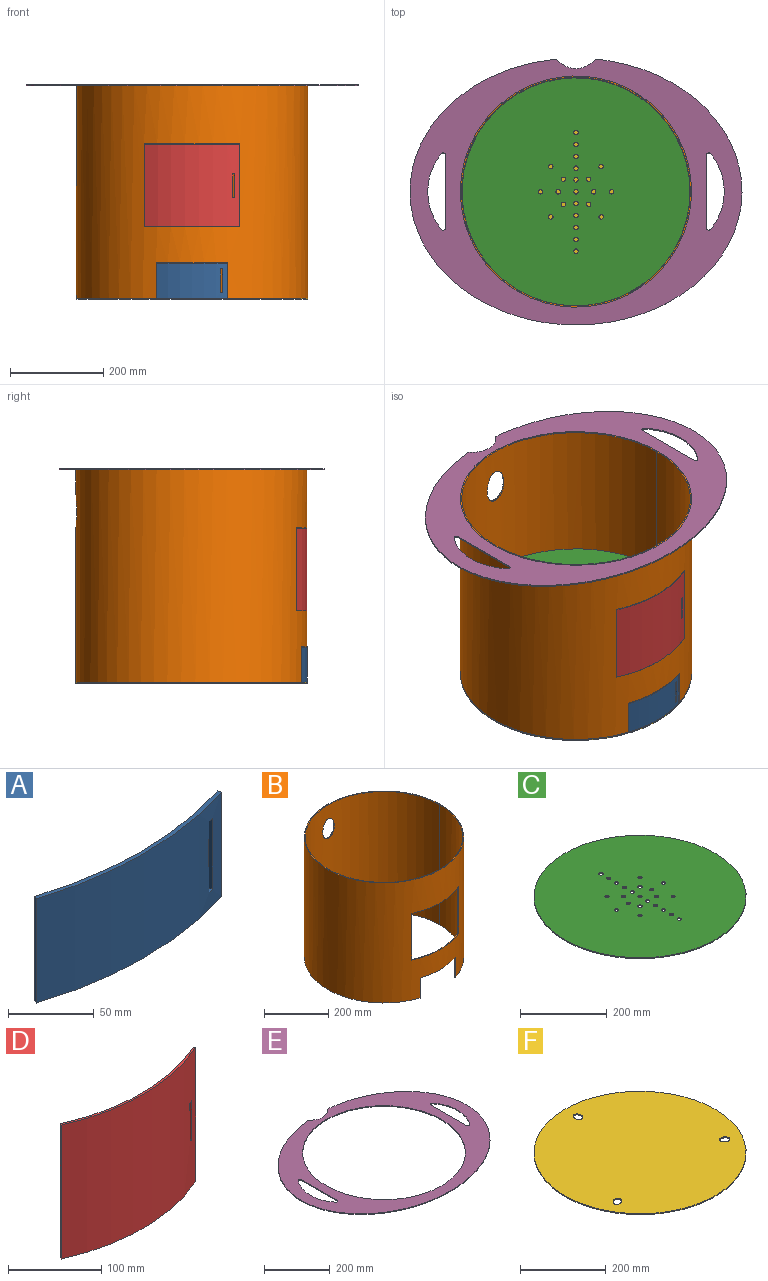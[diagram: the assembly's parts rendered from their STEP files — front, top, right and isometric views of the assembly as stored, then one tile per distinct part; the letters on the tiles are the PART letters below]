
ASSEMBLY  parts=6 mates=6
PART A: 10 faces, bbox 152.5x14.6x74.6 mm
  f0: plane 152.53x14.56mm, normal (0,0,-1), area 409.4mm2, adj f1,f7,f8,f9
  f1: plane 74.61x2.53mm, normal (0.95,0.31,0), area 198mm2, adj f0,f2,f8,f9
  f2: plane 152.53x14.56mm, normal (0,0,1), area 409.4mm2, adj f1,f7,f8,f9
  f3: plane 4.54x3.59mm, normal (0,0,-1), area 10.6mm2, adj f4,f6,f8,f9
  f4: plane 50.8x2.56mm, normal (-0.96,-0.27,0), area 134.8mm2, adj f3,f5,f8,f9
  f5: plane 4.54x3.59mm, normal (0,0,1), area 10.6mm2, adj f4,f6,f8,f9
  f6: plane 50.8x2.57mm, normal (0.97,0.25,0), area 134.8mm2, adj f3,f5,f8,f9
  f7: plane 74.61x2.53mm, normal (-0.95,0.31,0), area 198mm2, adj f0,f2,f8,f9
  f8: cylinder r=247.65mm len=152.53mm, axis (0,0,1), area 11365mm2, adj f0,f1,f2,f3,f4,f5,f6,f7
  f9: cylinder r=245mm len=150.9mm, axis (0,0,1), area 11243.2mm2, adj f0,f1,f2,f3,f4,f5,f6,f7
PART B: 18 faces, bbox 495.3x495.3x457.2 mm
  f0: plane 76.2x2.52mm, normal (0.95,-0.31,0), area 202.3mm2, adj f1,f15,f16,f17
  f1: plane 495.3x483.02mm, normal (0,0,-1), area 2873.6mm2, adj f0,f2,f16,f17
  f2: plane 457.2x2.65mm, normal (0,-1,0), area 1213.5mm2, adj f1,f3,f16,f17
  f3: plane 495.3x495.3mm, normal (0,0,1), area 4107.4mm2, adj f2,f4,f16,f17
  f4: plane 457.2x2.65mm, normal (0,1,0), area 1213.5mm2, adj f3,f5,f16,f17
  f5: plane 235.37x171.45mm, normal (0,0,-1), area 820.2mm2, adj f4,f6,f16,f17
  f6: plane 76.2x2.52mm, normal (-0.95,-0.31,0), area 202.3mm2, adj f5,f15,f16,f17
  f7: plane 205.4x24.71mm, normal (0,0,1), area 559.2mm2, adj f8,f14,f16,f17
  f8: plane 177.8x2.42mm, normal (-0.91,-0.41,0), area 471.9mm2, adj f7,f9,f16,f17
  f9: plane 205.4x24.71mm, normal (0,0,-1), area 559.2mm2, adj f8,f14,f16,f17
  f10: bspline ~51.37x40.16mm, area 281.1mm2, adj f11,f13,f16,f17
  f11: bspline ~2.66x1.89mm, area 5mm2, adj f10,f12,f16,f17
  f12: bspline ~50.3x32.47mm, area 235.5mm2, adj f11,f13,f16,f17
  f13: bspline ~2.99x2.67mm, area 8mm2, adj f10,f12,f16,f17
  f14: plane 177.8x2.42mm, normal (0.91,-0.41,0), area 471.9mm2, adj f7,f9,f16,f17
  f15: plane 154.05x14.81mm, normal (0,0,-1), area 413.6mm2, adj f0,f6,f16,f17
  f16: cylinder r=245mm len=489.99mm, axis (0,0,1), area 651624.3mm2, adj f0,f1,f2,f3,f4,f5,f6,f7
  f17: cylinder r=247.65mm len=495.3mm, axis (0,0,1), area 658667.2mm2, adj f0,f1,f2,f3,f4,f5,f6,f7
PART C: 26 faces, bbox 488.2x488.2x2.7 mm
  f0: cylinder r=4.76mm len=9.53mm, axis (0,0,1), area 79.4mm2, adj f24,f25
  f1: cylinder r=4.76mm len=9.53mm, axis (0,0,1), area 79.4mm2, adj f24,f25
  f2: cylinder r=4.76mm len=9.53mm, axis (0,0,1), area 79.4mm2, adj f24,f25
  f3: cylinder r=4.76mm len=9.53mm, axis (0,0,1), area 79.4mm2, adj f24,f25
  f4: cylinder r=4.76mm len=9.53mm, axis (0,0,1), area 79.4mm2, adj f24,f25
  f5: cylinder r=4.76mm len=9.53mm, axis (0,0,1), area 79.4mm2, adj f24,f25
  f6: cylinder r=4.76mm len=9.53mm, axis (0,0,1), area 79.4mm2, adj f24,f25
  f7: cylinder r=4.76mm len=9.53mm, axis (0,0,1), area 79.4mm2, adj f24,f25
  f8: cylinder r=4.76mm len=9.53mm, axis (0,0,1), area 79.4mm2, adj f24,f25
  f9: cylinder r=4.76mm len=9.53mm, axis (0,0,1), area 79.4mm2, adj f24,f25
  f10: cylinder r=4.76mm len=9.53mm, axis (0,0,1), area 79.4mm2, adj f24,f25
  f11: cylinder r=4.76mm len=9.53mm, axis (0,0,1), area 79.4mm2, adj f24,f25
  f12: cylinder r=4.76mm len=9.53mm, axis (0,0,1), area 79.4mm2, adj f24,f25
  f13: cylinder r=4.76mm len=9.53mm, axis (0,0,1), area 79.4mm2, adj f24,f25
  f14: cylinder r=4.76mm len=9.53mm, axis (0,0,1), area 79.4mm2, adj f24,f25
  f15: cylinder r=4.76mm len=9.53mm, axis (0,0,1), area 79.4mm2, adj f24,f25
  f16: cylinder r=4.76mm len=9.53mm, axis (0,0,1), area 79.4mm2, adj f24,f25
  f17: cylinder r=4.76mm len=9.53mm, axis (0,0,1), area 79.4mm2, adj f24,f25
  f18: cylinder r=4.76mm len=9.53mm, axis (0,0,1), area 79.4mm2, adj f24,f25
  f19: cylinder r=4.76mm len=9.53mm, axis (0,0,1), area 79.4mm2, adj f24,f25
  f20: cylinder r=4.76mm len=9.53mm, axis (0,0,1), area 79.4mm2, adj f24,f25
  f21: cylinder r=4.76mm len=9.53mm, axis (0,0,1), area 79.4mm2, adj f24,f25
  f22: cylinder r=4.76mm len=9.53mm, axis (0,0,1), area 79.4mm2, adj f24,f25
  f23: cylinder r=244.08mm len=488.16mm, axis (0,0,1), area 4070.6mm2, adj f24,f25
  f24: plane 488.16x488.16mm, normal (0,0,-1), area 185518.8mm2, adj f0,f1,f2,f3,f4,f5,f6,f7
  f25: plane 488.16x488.16mm, normal (0,0,1), area 185518.8mm2, adj f0,f1,f2,f3,f4,f5,f6,f7
PART D: 10 faces, bbox 203.9x24.4x176.2 mm
  f0: plane 203.95x24.39mm, normal (0,0,-1), area 554.9mm2, adj f1,f7,f8,f9
  f1: plane 176.21x2.42mm, normal (0.91,0.41,0), area 467.7mm2, adj f0,f2,f8,f9
  f2: plane 203.95x24.39mm, normal (0,0,1), area 554.9mm2, adj f1,f7,f8,f9
  f3: plane 5.09x4.08mm, normal (0,0,-1), area 11.8mm2, adj f4,f6,f8,f9
  f4: plane 50.8x2.47mm, normal (-0.93,-0.37,0), area 134.8mm2, adj f3,f5,f8,f9
  f5: plane 5.09x4.08mm, normal (0,0,1), area 11.8mm2, adj f4,f6,f8,f9
  f6: plane 50.8x2.48mm, normal (0.94,0.35,0), area 134.8mm2, adj f3,f5,f8,f9
  f7: plane 176.21x2.42mm, normal (-0.91,0.41,0), area 467.7mm2, adj f0,f2,f8,f9
  f8: cylinder r=247.65mm len=203.95mm, axis (0,0,1), area 36813.2mm2, adj f0,f1,f2,f3,f4,f5,f6,f7
  f9: cylinder r=245mm len=201.76mm, axis (0,0,1), area 36418.6mm2, adj f0,f1,f2,f3,f4,f5,f6,f7
PART E: 13 faces, bbox 711.2x569.6x2.7 mm
  f0: extruded ~710.03x569.62mm, area 5147.3mm2, adj f6,f7,f8
  f1: plane 155.34x2.65mm, normal (1,0,0), area 412.3mm2, adj f7,f8,f11,f12
  f2: cylinder r=127mm len=161.81mm, axis (0,0,1), area 465.6mm2, adj f7,f8,f9,f10
  f3: plane 155.34x2.65mm, normal (-1,0,0), area 412.3mm2, adj f7,f8,f9,f10
  f4: cylinder r=127mm len=161.81mm, axis (0,0,1), area 465.6mm2, adj f7,f8,f11,f12
  f5: cylinder r=247.65mm len=495.3mm, axis (0,0,1), area 4130.2mm2, adj f7,f8
  f6: cylinder r=50.8mm len=81.5mm, axis (0,0,1), area 251mm2, adj f0,f7,f8
  f7: plane 711.2x569.62mm, normal (0,0,-1), area 115896.4mm2, adj f0,f1,f2,f3,f4,f5,f6,f9
  f8: plane 711.2x569.62mm, normal (0,0,1), area 115896.4mm2, adj f0,f1,f2,f3,f4,f5,f6,f9
  f9: cylinder r=5.08mm len=9mm, axis (0,0,1), area 33mm2, adj f2,f3,f7,f8
  f10: cylinder r=5.08mm len=9mm, axis (0,0,1), area 33mm2, adj f2,f3,f7,f8
  f11: cylinder r=5.08mm len=9mm, axis (0,0,1), area 33mm2, adj f1,f4,f7,f8
  f12: cylinder r=5.08mm len=9mm, axis (0,0,1), area 33mm2, adj f1,f4,f7,f8
PART F: 15 faces, bbox 495.3x495.3x2.7 mm
  f0: plane 2.66x1.71mm, normal (1,0,0), area 4.3mm2, adj f1,f11,f13,f14
  f1: extruded ~19.81x11.62mm, area 89.6mm2, adj f0,f2,f13,f14
  f2: plane 2.66x1.72mm, normal (-1,0,0), area 4.1mm2, adj f1,f11,f13,f14
  f3: plane 2.66x1.48mm, normal (-0.5,0.87,0), area 4.3mm2, adj f4,f10,f13,f14
  f4: extruded ~18.98x16.18mm, area 89.6mm2, adj f3,f5,f13,f14
  f5: plane 2.66x1.49mm, normal (0.5,-0.87,0), area 4.1mm2, adj f4,f10,f13,f14
  f6: plane 2.66x1.48mm, normal (-0.5,-0.87,0), area 4.3mm2, adj f7,f9,f13,f14
  f7: extruded ~18.98x16.18mm, area 89.6mm2, adj f6,f8,f13,f14
  f8: plane 2.66x1.49mm, normal (0.5,0.87,0), area 4.1mm2, adj f7,f9,f13,f14
  f9: extruded ~18.8x16.03mm, area 88.4mm2, adj f6,f8,f13,f14
  f10: extruded ~18.89x15.86mm, area 88.4mm2, adj f3,f5,f13,f14
  f11: extruded ~19.81x11.44mm, area 88.4mm2, adj f0,f2,f13,f14
  f12: cylinder r=247.65mm len=495.3mm, axis (0,0,1), area 4130.2mm2, adj f13,f14
  f13: plane 495.3x495.3mm, normal (0,0,-1), area 191516.5mm2, adj f0,f1,f2,f3,f4,f5,f6,f7
  f14: plane 495.3x495.3mm, normal (0,0,1), area 191516.1mm2, adj f0,f1,f2,f3,f4,f5,f6,f7
PLACE A rot(axis=(0,0,-1),0deg) t=(-0.2,0.35,2.03)mm
PLACE B t=(-0.2,0.35,230.63)mm
PLACE C t=(-0.2,0.35,151.77)mm
PLACE D rot(axis=(0,0,1),0deg) t=(-0.2,0.35,154.43)mm
PLACE E t=(-0.2,0.35,456.57)mm
PLACE F t=(-0.2,0.35,-0.63)mm fixed
MATE revolute D.f8 <-> C.f23  axis (0,0,-1) through (-0.2,0.35,154.43)mm
MATE revolute A.f8 <-> F.f12  axis (0,0,-1) through (-0.2,0.35,2.03)mm
MATE planar C.f23 <-> B.f7  axis (0,0,1) through (-0.2,0.35,154.43)mm
MATE fastened B.f16 <-> E.f5  axis (0,0,1) through (-0.2,0.35,459.23)mm
MATE fastened B.f16 <-> F.f12  axis (0,0,-1) through (-0.2,0.35,2.03)mm
MATE slider C.f23 <-> B.f16  axis (0,0,1) through (-0.2,0.35,154.43)mm
